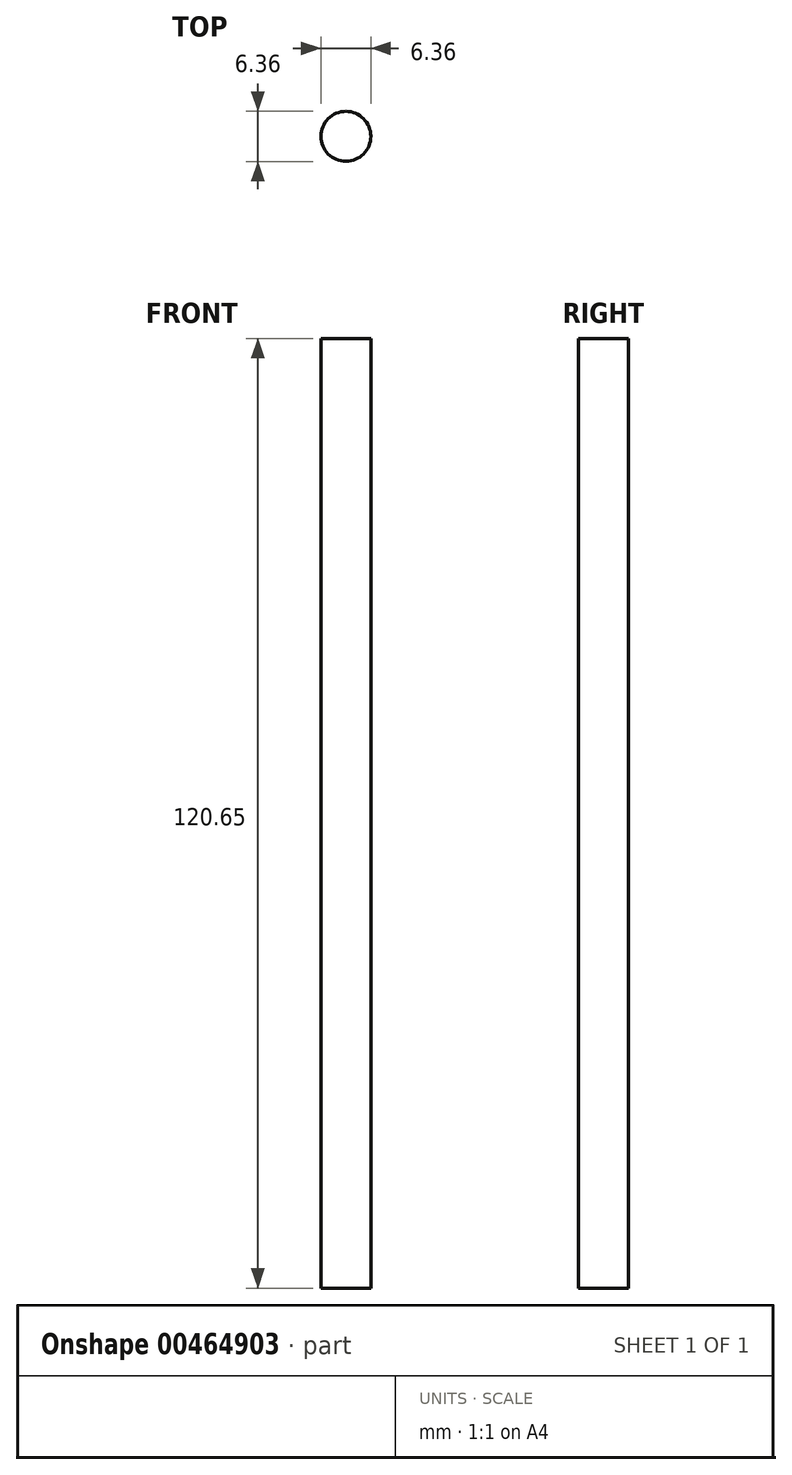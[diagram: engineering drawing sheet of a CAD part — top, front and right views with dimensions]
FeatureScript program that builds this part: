
annotation { "Feature Type Name" : "Feature", "Feature Type Description" : "" }
export const myFeature = defineFeature(function(context is Context, id is Id, definition is map)
    precondition{}
    {
        {
            var Q0;
            Q0=qCreatedBy(makeId("Top.planeOp"),FACE);
            var sketch = newSketch(context, id + "F0", { "sketchPlane" : qUnion([Q0])});
            skCircle(sketch, "E0", {"center": v(0, 0) * mm, "radius": 3.18 * mm});
            skSolve(sketch);
        }
        {
            var Q0;
            Q0=makeQuery(id+"F0.imprint","IMPRINT",FACE,{"disambiguationData":[TD([[makeQuery(id+"F0.imprint","IMPRINT",EDGE,{"derivedFrom":sQuery(id+"F0.wireOp",EDGE,"E0")}),1.0]])]});
            extrude(context, id + "F1", {"entities" : qUnion([Q0]), "depth" : 120.65 * mm});
        }
    });
